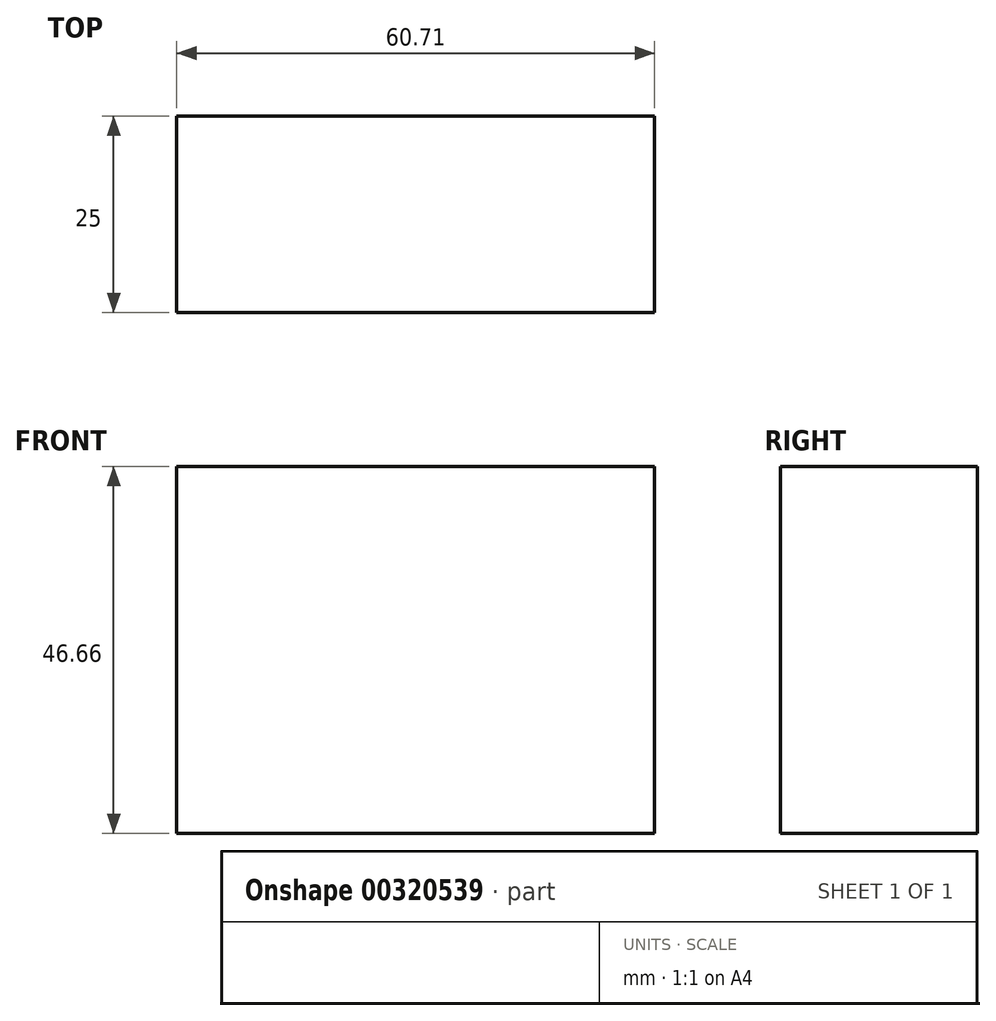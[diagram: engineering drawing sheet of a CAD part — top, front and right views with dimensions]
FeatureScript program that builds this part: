
annotation { "Feature Type Name" : "Feature", "Feature Type Description" : "" }
export const myFeature = defineFeature(function(context is Context, id is Id, definition is map)
    precondition{}
    {
        {
            var Q0;
            Q0=qCreatedBy(makeId("Front.planeOp"),FACE);
            var sketch = newSketch(context, id + "F0", { "sketchPlane" : qUnion([Q0])});
            skLineSegment(sketch, "E0.bottom", {"start": v(-62.96, 0) * mm, "end": v(-2.25, 0) * mm});
            skLineSegment(sketch, "E0.top", {"start": v(-62.96, 46.66) * mm, "end": v(-2.25, 46.66) * mm});
            skLineSegment(sketch, "E0.left", {"start": v(-62.96, 0) * mm, "end": v(-62.96, 46.66) * mm});
            skLineSegment(sketch, "E0.right", {"start": v(-2.25, 0) * mm, "end": v(-2.25, 46.66) * mm});
            skPoint(sketch, "E0.middle", {"position": v(-32.6, 23.33) * mm});
            skSolve(sketch);
        }
        {
            var Q0;
            Q0=makeQuery(id+"F0.imprint","IMPRINT",FACE,{"disambiguationData":[TD([[makeQuery(id+"F0.imprint","IMPRINT",EDGE,{"derivedFrom":sQuery(id+"F0.wireOp",EDGE,"E0.bottom")}),1.0]])]});
            extrude(context, id + "F1", {"entities" : qUnion([Q0]), "depth" : 25 * mm});
        }
    });
